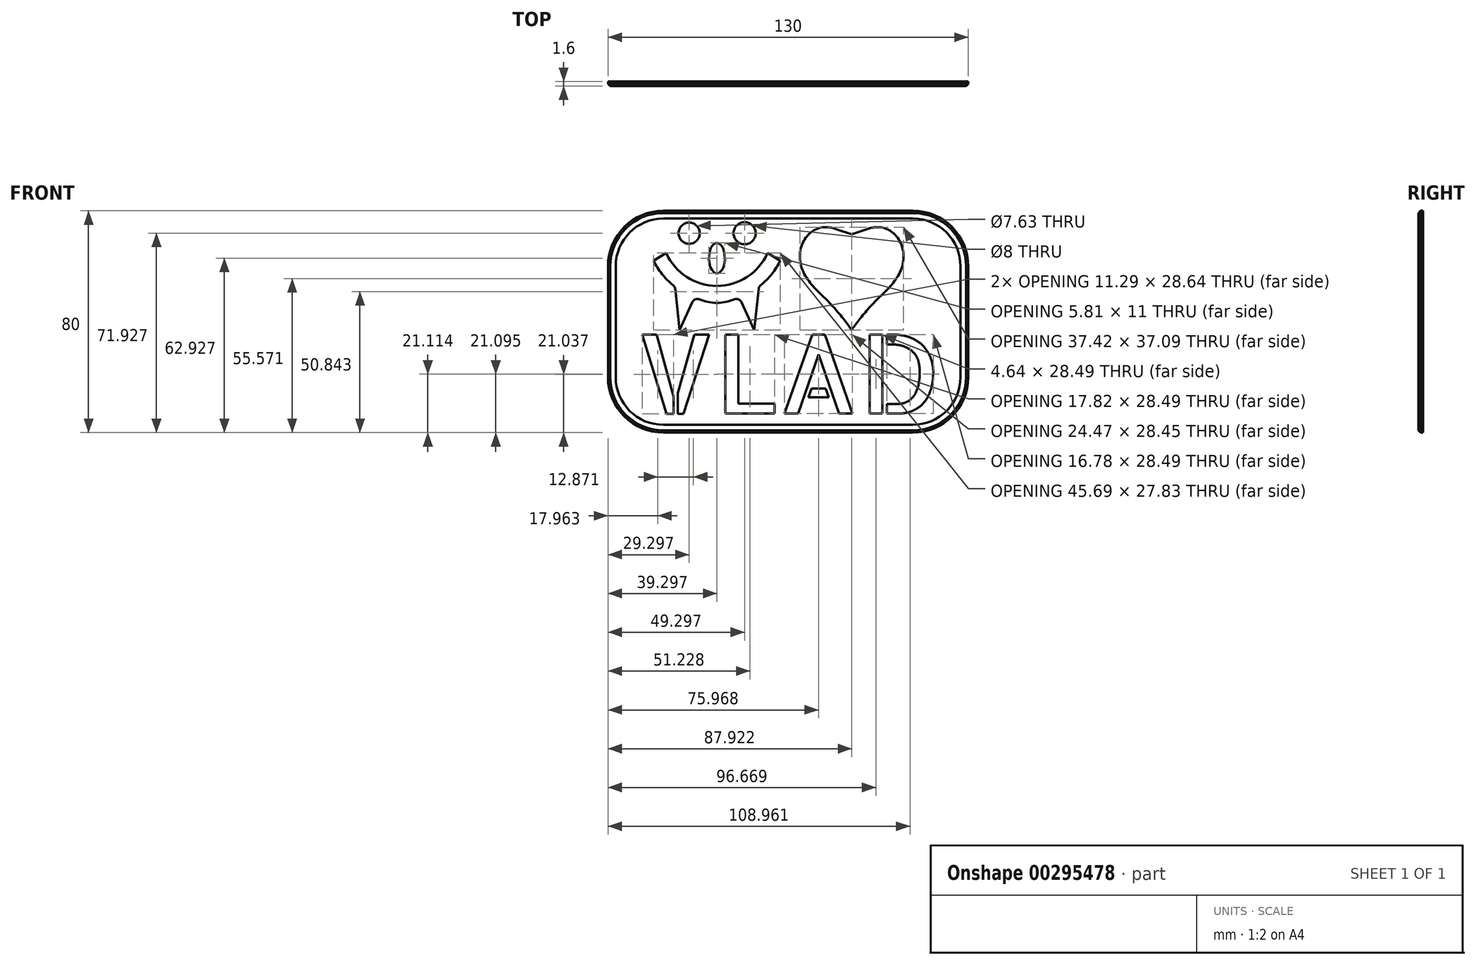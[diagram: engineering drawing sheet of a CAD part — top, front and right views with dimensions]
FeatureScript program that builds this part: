
annotation { "Feature Type Name" : "Feature", "Feature Type Description" : "" }
export const myFeature = defineFeature(function(context is Context, id is Id, definition is map)
    precondition{}
    {
        {
            var Q0;
            Q0=qCreatedBy(makeId("Front.planeOp"),FACE);
            var sketch = newSketch(context, id + "F0", { "sketchPlane" : qUnion([Q0])});
            skLineSegment(sketch, "E0.bottom", {"start": v(-65, 60) * mm, "end": v(65, 60) * mm});
            skLineSegment(sketch, "E0.top", {"start": v(-65, -20) * mm, "end": v(65, -20) * mm});
            skLineSegment(sketch, "E0.left", {"start": v(-65, 60) * mm, "end": v(-65, -20) * mm});
            skLineSegment(sketch, "E0.right", {"start": v(65, 60) * mm, "end": v(65, -20) * mm});
            skSolve(sketch);
        }
        {
            var Q0;
            Q0=qSketchRegion(id+"F0",true);
            extrude(context, id + "F1", {"entities" : qUnion([Q0]), "depth" : 1.6 * mm});
        }
        {
            var Q0;
            Q0=makeQuery(id+"F1.opExtrude","CAP_FACE",FACE,{"disambiguationData":[OSD([sQuery(id+"F0.wireOp",EDGE,"E0.bottom"),sQuery(id+"F0.wireOp",EDGE,"E0.top"),sQuery(id+"F0.wireOp",EDGE,"E0.left"),sQuery(id+"F0.wireOp",EDGE,"E0.right")])],"isStart":false});
            var sketch = newSketch(context, id + "F2", { "sketchPlane" : qUnion([Q0])});
            skText(sketch, "E1", { "text": "VLAD", "fontName": "AllertaStencil-Regular.ttf"});
            skText(sketch, "E2", { "text": "♥", "fontName": "NotoSansCJKjp-Regular.otf"});
            const initialGuessF2  = {"E1": [-0.055, -0.01313, 1, 0, 0.0285], "E2": [0.0007, 0.01874, 1, 0, 0.032]};
            skSetInitialGuess(sketch, initialGuessF2);
            skSolve(sketch);
        }
        {
            var Q0;
            Q0=qSketchRegion(id+"F2",true);
            extrude(context, id + "F3", {"entities" : qUnion([Q0]), "operationType" : NewBodyOperationType.REMOVE, "endBound" : BoundingType.THROUGH_ALL, "oppositeDirection" : true, "depth" : 25 * mm});
        }
        {
            var Q0;
            Q0=makeQuery(id+"F1.opExtrude","SWEPT_EDGE",EDGE,{"disambiguationData":[OSD([sQuery(id+"F0.wireOp",EDGE,"E0.top"),sQuery(id+"F0.wireOp",EDGE,"E0.right")])]});
            var Q1;
            Q1=makeQuery(id+"F1.opExtrude","SWEPT_EDGE",EDGE,{"disambiguationData":[OSD([sQuery(id+"F0.wireOp",EDGE,"E0.bottom"),sQuery(id+"F0.wireOp",EDGE,"E0.right")])]});
            var Q2;
            Q2=makeQuery(id+"F1.opExtrude","SWEPT_EDGE",EDGE,{"disambiguationData":[OSD([sQuery(id+"F0.wireOp",EDGE,"E0.top"),sQuery(id+"F0.wireOp",EDGE,"E0.left")])]});
            var Q3;
            Q3=makeQuery(id+"F1.opExtrude","SWEPT_EDGE",EDGE,{"disambiguationData":[OSD([sQuery(id+"F0.wireOp",EDGE,"E0.bottom"),sQuery(id+"F0.wireOp",EDGE,"E0.left")])]});
            fillet(context, id + "F4", {"entities" : qUnion([Q0, Q1, Q2, Q3]), "radius" : 20 * mm, "tangentPropagation" : true, "allowEdgeOverflow" : false});
        }
        {
            var Q0;
            Q0=makeQuery(id+"F1.opExtrude","CAP_EDGE",EDGE,{"disambiguationData":[OSD([sQuery(id+"F0.wireOp",EDGE,"E0.top")])],"isStart":false});
            chamfer(context, id + "F5", {"entities" : qUnion([Q0]), "width" : 0.8 * mm, "tangentPropagation" : true});
        }
        {
            var Q0;
            Q0=makeQuery(id+"F1.opExtrude","CAP_FACE",FACE,{"disambiguationData":[OSD([sQuery(id+"F0.wireOp",EDGE,"E0.bottom"),sQuery(id+"F0.wireOp",EDGE,"E0.top"),sQuery(id+"F0.wireOp",EDGE,"E0.left"),sQuery(id+"F0.wireOp",EDGE,"E0.right")])],"isStart":false});
            var sketch = newSketch(context, id + "F6", { "sketchPlane" : qUnion([Q0])});
            skCircle(sketch, "E3", {"center": v(-35.7, 51.93) * mm, "radius": 3.82 * mm});
            skCircle(sketch, "E4", {"center": v(-15.7, 51.93) * mm, "radius": 4 * mm});
            skEllipse(sketch, "E5", {"center": v(-25.7, 42.93) * mm, "majorRadius": 5.5 * mm, "minorRadius": 2.9 * mm, "majorAxis": v(0, 1)});
            skArc(sketch, "E6", {"start": v(-41.7, 40.93) * mm, "mid": v(-25.7, 32.93) * mm, "end": v(-9.7, 40.93) * mm});
            skLineSegment(sketch, "E7", {"start": v(-40.84, 32.66) * mm, "end": v(-39.2, 16.93) * mm});
            skLineSegment(sketch, "E8", {"start": v(-39.2, 16.93) * mm, "end": v(-33.7, 28.93) * mm});
            skLineSegment(sketch, "E9", {"start": v(-25.7, 42.93) * mm, "end": v(-25.7, 20.3) * mm, "construction": true});
            skLineSegment(sketch, "E10", {"start": v(-10.56, 32.66) * mm, "end": v(-12.2, 16.93) * mm});
            skLineSegment(sketch, "E11", {"start": v(-12.2, 16.93) * mm, "end": v(-17.7, 28.93) * mm});
            skArc(sketch, "E12", {"start": v(-33.7, 28.93) * mm, "mid": v(-25.7, 26.8) * mm, "end": v(-17.7, 28.93) * mm});
            skArc(sketch, "E13", {"start": v(-10.56, 32.66) * mm, "mid": v(-6.14, 36.89) * mm, "end": v(-2.86, 42.06) * mm});
            skArc(sketch, "E14", {"start": v(-9.7, 40.93) * mm, "mid": v(-8.47, 42.78) * mm, "end": v(-7.45, 44.76) * mm});
            skLineSegment(sketch, "E15", {"start": v(-7.45, 44.76) * mm, "end": v(-2.86, 42.06) * mm});
            skArc(sketch, "E16.MirrorCS", {"start": v(-40.84, 32.66) * mm, "mid": v(-45.27, 36.89) * mm, "end": v(-48.55, 42.06) * mm});
            skLineSegment(sketch, "E17.MirrorCS", {"start": v(-43.96, 44.76) * mm, "end": v(-48.55, 42.06) * mm});
            skArc(sketch, "E18.MirrorCS", {"start": v(-41.7, 40.93) * mm, "mid": v(-42.94, 42.78) * mm, "end": v(-43.96, 44.76) * mm});
            skSolve(sketch);
        }
        {
            var Q0;
            Q0=qSketchRegion(id+"F6",true);
            extrude(context, id + "F7", {"entities" : qUnion([Q0]), "operationType" : NewBodyOperationType.REMOVE, "endBound" : BoundingType.THROUGH_ALL, "oppositeDirection" : true, "depth" : 25 * mm});
        }
        {
            var Q0;
            Q0=makeQuery(id+"F1.opExtrude","CAP_FACE",FACE,{"disambiguationData":[OSD([sQuery(id+"F0.wireOp",EDGE,"E0.bottom"),sQuery(id+"F0.wireOp",EDGE,"E0.top"),sQuery(id+"F0.wireOp",EDGE,"E0.left"),sQuery(id+"F0.wireOp",EDGE,"E0.right")])],"isStart":false});
            var sketch = newSketch(context, id + "F8", { "sketchPlane" : qUnion([Q0])});
            skLineSegment(sketch, "E19.0", {"start": v(-45, -17.2) * mm, "end": v(45, -17.2) * mm});
            skArc(sketch, "E19.1", {"start": v(-62.2, 0) * mm, "mid": v(-57.16, -12.16) * mm, "end": v(-45, -17.2) * mm});
            skArc(sketch, "E19.2", {"start": v(45, -17.2) * mm, "mid": v(57.16, -12.16) * mm, "end": v(62.2, 0) * mm});
            skLineSegment(sketch, "E19.3", {"start": v(-62.2, 40) * mm, "end": v(-62.2, 0) * mm});
            skLineSegment(sketch, "E19.4", {"start": v(62.2, 0) * mm, "end": v(62.2, 40) * mm});
            skArc(sketch, "E19.5", {"start": v(62.2, 40) * mm, "mid": v(57.16, 52.16) * mm, "end": v(45, 57.2) * mm});
            skLineSegment(sketch, "E19.6", {"start": v(45, 57.2) * mm, "end": v(-45, 57.2) * mm});
            skArc(sketch, "E19.7", {"start": v(-45, 57.2) * mm, "mid": v(-57.16, 52.16) * mm, "end": v(-62.2, 40) * mm});
            skSolve(sketch);
        }
        {
            var Q0;
            Q0=qSketchRegion(id+"F8",true);
            extrude(context, id + "F9", {"entities" : qUnion([Q0]), "operationType" : NewBodyOperationType.REMOVE, "oppositeDirection" : true, "depth" : 0.4 * mm});
        }
        {
            var Q0;
            Q0=makeQuery(id+"F9.boolean.opBoolean","COPY",FACE,{"derivedFrom":makeQuery(id+"F9.opExtrude","CAP_FACE",FACE,{"disambiguationData":[OSD([sQuery(id+"F8.wireOp",EDGE,"E19.0"),sQuery(id+"F8.wireOp",EDGE,"E19.1"),sQuery(id+"F8.wireOp",EDGE,"E19.2"),sQuery(id+"F8.wireOp",EDGE,"E19.3"),sQuery(id+"F8.wireOp",EDGE,"E19.4"),sQuery(id+"F8.wireOp",EDGE,"E19.5"),sQuery(id+"F8.wireOp",EDGE,"E19.6"),sQuery(id+"F8.wireOp",EDGE,"E19.7")])],"isStart":false})});
            var sketch = newSketch(context, id + "F10", { "sketchPlane" : qUnion([Q0])});
            skLineSegment(sketch, "E20", {"start": v(28.92, 53.56) * mm, "end": v(22.93, 51.5) * mm});
            skLineSegment(sketch, "E21", {"start": v(22.93, 51.5) * mm, "end": v(16.92, 53.57) * mm});
            skLineSegment(sketch, "E22", {"start": v(16.92, 53.57) * mm, "end": v(16.92, 45.28) * mm});
            skLineSegment(sketch, "E23", {"start": v(16.92, 45.28) * mm, "end": v(29.17, 45.28) * mm});
            skLineSegment(sketch, "E24", {"start": v(29.17, 45.28) * mm, "end": v(28.92, 53.56) * mm});
            skSolve(sketch);
        }
        {
            var Q0;
            Q0=qSketchRegion(id+"F10",true);
            extrude(context, id + "F11", {"entities" : qUnion([Q0]), "operationType" : NewBodyOperationType.REMOVE, "oppositeDirection" : true, "depth" : 25 * mm});
        }
        {
            var Q0;
            Q0=makeQuery(id+"F7.boolean.opBoolean","COPY",EDGE,{"derivedFrom":makeQuery(id+"F7.opExtrude","SWEPT_EDGE",EDGE,{"disambiguationData":[OSD([sQuery(id+"F6.wireOp",EDGE,"E7"),sQuery(id+"F6.wireOp",EDGE,"E16.MirrorCS")])]})});
            var Q1;
            Q1=makeQuery(id+"F7.boolean.opBoolean","COPY",EDGE,{"derivedFrom":makeQuery(id+"F7.opExtrude","SWEPT_EDGE",EDGE,{"disambiguationData":[OSD([sQuery(id+"F6.wireOp",EDGE,"E10"),sQuery(id+"F6.wireOp",EDGE,"E13")])]})});
            var Q2;
            Q2=makeQuery(id+"F7.boolean.opBoolean","COPY",EDGE,{"derivedFrom":makeQuery(id+"F7.opExtrude","SWEPT_EDGE",EDGE,{"disambiguationData":[OSD([sQuery(id+"F6.wireOp",EDGE,"E11"),sQuery(id+"F6.wireOp",EDGE,"E12")])]})});
            var Q3;
            Q3=makeQuery(id+"F7.boolean.opBoolean","COPY",EDGE,{"derivedFrom":makeQuery(id+"F7.opExtrude","SWEPT_EDGE",EDGE,{"disambiguationData":[OSD([sQuery(id+"F6.wireOp",EDGE,"E8"),sQuery(id+"F6.wireOp",EDGE,"E12")])]})});
            fillet(context, id + "F12", {"entities" : qUnion([Q0, Q1, Q2, Q3]), "radius" : 2 * mm, "tangentPropagation" : true, "allowEdgeOverflow" : false});
        }
    });
